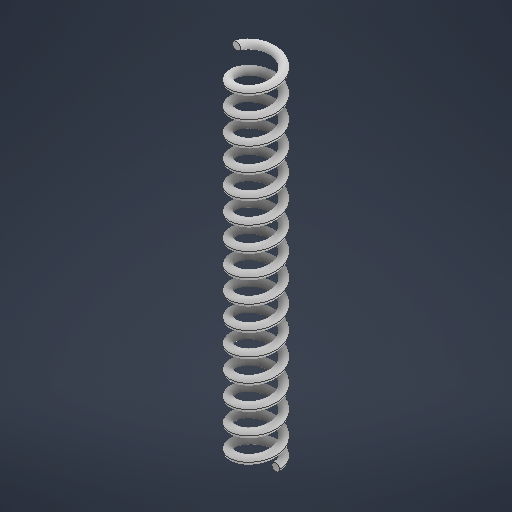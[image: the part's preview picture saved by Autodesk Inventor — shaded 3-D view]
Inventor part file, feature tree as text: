
AUTODESK INVENTOR PART (.ipt)
format: ipt  version: 2025.2 (Build 292293000, 293)  size: 715,776 bytes
history: native  units: mm
features: helix x1, sketch x1
ambient origin geometry x8: Origin, YZ Plane, XZ Plane, XY Plane, X Axis, Y Axis, Z Axis, Center Point
bodies: Solid1 (feature_tree)
feature tree (2):
  helix  "Coil1"  [1 undecoded]
  sketch  "Sketch2"  dims[d1=5.0mm d2=2.0mm d3=5.8mm d4=10.0mm d5=150.0mm d6=0.0mm d7=90.0deg d8=90.0deg d9=0.0mm d10=0.0mm]
note: 1 required parameter value undecoded (feature->parameter linkage not recoverable at this tier; creation-order binding heuristic only, values carry confidence <= 0.55)
